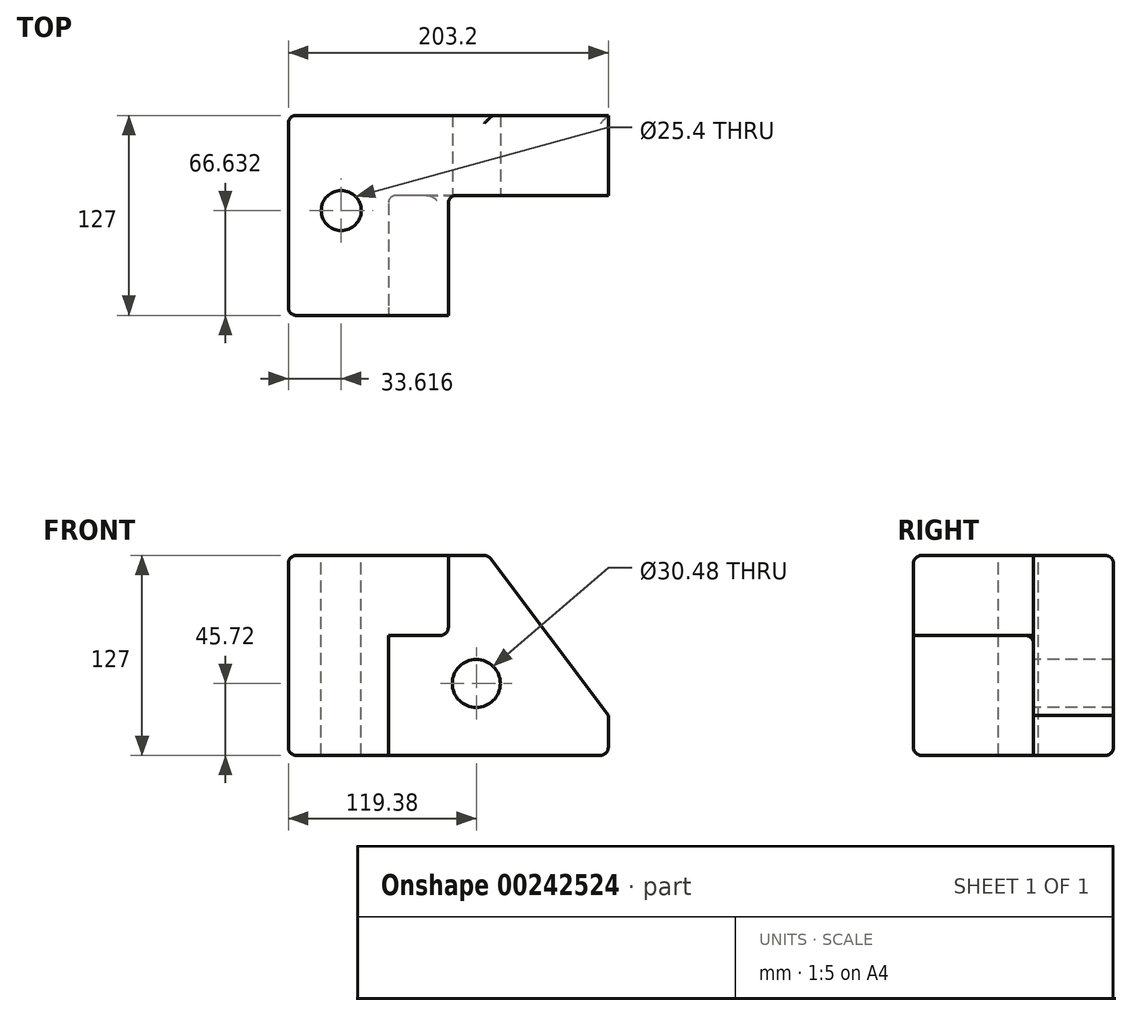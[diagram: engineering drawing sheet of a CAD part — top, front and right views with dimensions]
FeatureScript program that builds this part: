
annotation { "Feature Type Name" : "Feature", "Feature Type Description" : "" }
export const myFeature = defineFeature(function(context is Context, id is Id, definition is map)
    precondition{}
    {
        {
            var Q0;
            Q0=qCreatedBy(makeId("Front.planeOp"),FACE);
            var sketch = newSketch(context, id + "F0", { "sketchPlane" : qUnion([Q0])});
            skLineSegment(sketch, "E0.bottom", {"start": v(101.6, -63.5) * mm, "end": v(-101.6, -63.5) * mm});
            skLineSegment(sketch, "E0.top", {"start": v(101.6, 63.5) * mm, "end": v(-101.6, 63.5) * mm});
            skLineSegment(sketch, "E0.left", {"start": v(101.6, -63.5) * mm, "end": v(101.6, 63.5) * mm});
            skLineSegment(sketch, "E0.right", {"start": v(-101.6, -63.5) * mm, "end": v(-101.6, 63.5) * mm});
            skPoint(sketch, "E0.middle", {"position": v(0, 0) * mm});
            skSolve(sketch);
        }
        {
            var Q0;
            Q0 = qSketchRegion(id + "F0", true);
            extrude(context, id + "F1", {"entities" : qUnion([Q0]), "depth" : 127 * mm});
        }
        {
            var Q0;
            Q0=makeQuery(id+"F1.opExtrude","CAP_FACE",FACE,{"disambiguationData":[OSD([sQuery(id+"F0.wireOp",EDGE,"E0.bottom"),sQuery(id+"F0.wireOp",EDGE,"E0.top"),sQuery(id+"F0.wireOp",EDGE,"E0.left"),sQuery(id+"F0.wireOp",EDGE,"E0.right")])],"isStart":false});
            var sketch = newSketch(context, id + "F2", { "sketchPlane" : qUnion([Q0])});
            skLineSegment(sketch, "E1", {"start": v(-101.6, 63.5) * mm, "end": v(0, 63.5) * mm});
            skLineSegment(sketch, "E2", {"start": v(0, 63.5) * mm, "end": v(0, 12.7) * mm});
            skLineSegment(sketch, "E3", {"start": v(0, 12.7) * mm, "end": v(-38.1, 12.7) * mm});
            skLineSegment(sketch, "E4", {"start": v(-38.1, 12.7) * mm, "end": v(-38.1, -63.5) * mm});
            skLineSegment(sketch, "E5", {"start": v(-38.1, -63.5) * mm, "end": v(-101.6, -63.5) * mm});
            skLineSegment(sketch, "E6", {"start": v(-101.6, -63.5) * mm, "end": v(-101.6, 63.5) * mm});
            skSolve(sketch);
        }
        {
            var Q0;
            {var subQ3=sQuery(id+"F2.wireOp",EDGE,"E2");Q0=makeQuery(id+"F2.imprint","IMPRINT",FACE,{"disambiguationData":[TD([[makeQuery(id+"F2.imprint","IMPRINT",EDGE,{"derivedFrom":subQ3}),1.0]])]});}
            extrude(context, id + "F3", {"entities" : qUnion([Q0]), "operationType" : NewBodyOperationType.REMOVE, "oppositeDirection" : true, "depth" : 76.2 * mm});
        }
        {
            var Q0;
            Q0=makeQuery(id+"F1.opExtrude","SWEPT_EDGE",EDGE,{"disambiguationData":[OSD([sQuery(id+"F0.wireOp",EDGE,"E0.top"),sQuery(id+"F0.wireOp",EDGE,"E0.left")])]});
            chamfer(context, id + "F4", {"entities" : qUnion([Q0]), "chamferType" : ChamferType.TWO_OFFSETS, "width1" : 76.2 * mm, "oppositeDirection" : false, "width2" : 101.6 * mm, "tangentPropagation" : true});
        }
        {
            var Q0;
            Q0=makeQuery(id+"F3.boolean.opBoolean","COPY",EDGE,{"derivedFrom":makeQuery(id+"F3.opExtrude","SWEPT_EDGE",EDGE,{"disambiguationData":[OSD([sQuery(id+"F0.wireOp",EDGE,"E0.top"),sQuery(id+"F2.wireOp",EDGE,"E1"),sQuery(id+"F2.wireOp",EDGE,"E2")])]})});
            var Q1;
            Q1=makeQuery(id+"F3.boolean.opBoolean","COPY",EDGE,{"derivedFrom":makeQuery(id+"F3.opExtrude","CAP_EDGE",EDGE,{"disambiguationData":[OSD([sQuery(id+"F0.wireOp",EDGE,"E0.top")])],"isStart":false})});
            var Q2;
            {var subQ0=sQuery(id+"F0.wireOp",EDGE,"E0.top");Q2=makeQuery(id+"F4.opChamfer","BLEND_EDGE",EDGE,{"blendedFrom":[makeQuery(id+"F1.opExtrude","SWEPT_EDGE",EDGE,{"disambiguationData":[OSD([subQ0,sQuery(id+"F0.wireOp",EDGE,"E0.left")])]}),makeQuery(id+"F1.opExtrude","SWEPT_FACE",FACE,{"disambiguationData":[OSD([subQ0])]})],"blendedInto":[makeQuery(id+"F1.opExtrude","SWEPT_FACE",FACE,{"disambiguationData":[OSD([subQ0])]})]});}
            var Q3;
            Q3=makeQuery(id+"F1.opExtrude","CAP_EDGE",EDGE,{"disambiguationData":[OSD([sQuery(id+"F0.wireOp",EDGE,"E0.top")])],"isStart":true});
            var Q4;
            Q4=makeQuery(id+"F1.opExtrude","SWEPT_EDGE",EDGE,{"disambiguationData":[OSD([sQuery(id+"F0.wireOp",EDGE,"E0.top"),sQuery(id+"F0.wireOp",EDGE,"E0.right")])]});
            var Q5;
            Q5=makeQuery(id+"F1.opExtrude","CAP_EDGE",EDGE,{"disambiguationData":[OSD([sQuery(id+"F0.wireOp",EDGE,"E0.top")])],"isStart":false});
            var Q6;
            Q6=makeQuery(id+"F3.boolean.opBoolean","COPY",EDGE,{"derivedFrom":makeQuery(id+"F3.opExtrude","CAP_EDGE",EDGE,{"disambiguationData":[OSD([sQuery(id+"F2.wireOp",EDGE,"E2")])],"isStart":true})});
            var Q7;
            Q7=makeQuery(id+"F3.boolean.opBoolean","COPY",EDGE,{"derivedFrom":makeQuery(id+"F3.opExtrude","SWEPT_EDGE",EDGE,{"disambiguationData":[OSD([sQuery(id+"F2.wireOp",EDGE,"E2"),sQuery(id+"F2.wireOp",EDGE,"E3")])]})});
            var Q8;
            Q8=makeQuery(id+"F3.boolean.opBoolean","COPY",EDGE,{"derivedFrom":makeQuery(id+"F3.opExtrude","CAP_EDGE",EDGE,{"disambiguationData":[OSD([sQuery(id+"F2.wireOp",EDGE,"E2")])],"isStart":false})});
            var Q9;
            Q9=makeQuery(id+"F3.boolean.opBoolean","COPY",EDGE,{"derivedFrom":makeQuery(id+"F3.opExtrude","CAP_EDGE",EDGE,{"disambiguationData":[OSD([sQuery(id+"F2.wireOp",EDGE,"E4")])],"isStart":false})});
            var Q10;
            Q10=makeQuery(id+"F3.boolean.opBoolean","COPY",EDGE,{"derivedFrom":makeQuery(id+"F3.opExtrude","CAP_EDGE",EDGE,{"disambiguationData":[OSD([sQuery(id+"F2.wireOp",EDGE,"E4")])],"isStart":true})});
            var Q11;
            Q11=makeQuery(id+"F3.boolean.opBoolean","COPY",EDGE,{"derivedFrom":makeQuery(id+"F3.opExtrude","SWEPT_EDGE",EDGE,{"disambiguationData":[OSD([sQuery(id+"F0.wireOp",EDGE,"E0.bottom"),sQuery(id+"F2.wireOp",EDGE,"E4"),sQuery(id+"F2.wireOp",EDGE,"E5")])]})});
            var Q12;
            Q12=makeQuery(id+"F1.opExtrude","CAP_EDGE",EDGE,{"disambiguationData":[OSD([sQuery(id+"F0.wireOp",EDGE,"E0.bottom")])],"isStart":false});
            var Q13;
            Q13=makeQuery(id+"F1.opExtrude","CAP_EDGE",EDGE,{"disambiguationData":[OSD([sQuery(id+"F0.wireOp",EDGE,"E0.right")])],"isStart":false});
            var Q14;
            Q14=makeQuery(id+"F3.boolean.opBoolean","COPY",EDGE,{"derivedFrom":makeQuery(id+"F3.opExtrude","CAP_EDGE",EDGE,{"disambiguationData":[OSD([sQuery(id+"F0.wireOp",EDGE,"E0.bottom")])],"isStart":false})});
            var Q15;
            Q15=makeQuery(id+"F1.opExtrude","SWEPT_EDGE",EDGE,{"disambiguationData":[OSD([sQuery(id+"F0.wireOp",EDGE,"E0.bottom"),sQuery(id+"F0.wireOp",EDGE,"E0.left")])]});
            var Q16;
            Q16=makeQuery(id+"F1.opExtrude","SWEPT_EDGE",EDGE,{"disambiguationData":[OSD([sQuery(id+"F0.wireOp",EDGE,"E0.bottom"),sQuery(id+"F0.wireOp",EDGE,"E0.right")])]});
            var Q17;
            Q17=makeQuery(id+"F1.opExtrude","CAP_EDGE",EDGE,{"disambiguationData":[OSD([sQuery(id+"F0.wireOp",EDGE,"E0.right")])],"isStart":true});
            var Q18;
            Q18=makeQuery(id+"F1.opExtrude","CAP_EDGE",EDGE,{"disambiguationData":[OSD([sQuery(id+"F0.wireOp",EDGE,"E0.bottom")])],"isStart":true});
            fillet(context, id + "F5", {"entities" : qUnion([Q0, Q1, Q2, Q3, Q4, Q5, Q6, Q7, Q8, Q9, Q10, Q11, Q12, Q13, Q14, Q15, Q16, Q17, Q18]), "radius" : 5.08 * mm, "tangentPropagation" : true, "allowEdgeOverflow" : false});
        }
        {
            var Q0;
            Q0=makeQuery(id+"F3.boolean.opBoolean","COPY",FACE,{"derivedFrom":makeQuery(id+"F3.opExtrude","CAP_FACE",FACE,{"disambiguationData":[OSD([sQuery(id+"F0.wireOp",EDGE,"E0.bottom"),sQuery(id+"F0.wireOp",EDGE,"E0.top"),sQuery(id+"F0.wireOp",EDGE,"E0.left"),sQuery(id+"F2.wireOp",EDGE,"E2"),sQuery(id+"F2.wireOp",EDGE,"E3"),sQuery(id+"F2.wireOp",EDGE,"E4")])],"isStart":false})});
            var sketch = newSketch(context, id + "F6", { "sketchPlane" : qUnion([Q0])});
            skCircle(sketch, "E7", {"center": v(17.78, -17.78) * mm, "radius": 15.24 * mm});
            skSolve(sketch);
        }
        {
            var Q0;
            Q0=makeQuery(id+"F6.imprint","IMPRINT",FACE,{"disambiguationData":[TD([[makeQuery(id+"F6.imprint","IMPRINT",EDGE,{"derivedFrom":sQuery(id+"F6.wireOp",EDGE,"E7")}),1.0]])]});
            var Q1;
            Q1=makeQuery(id+"F1.opExtrude","CAP_FACE",FACE,{"disambiguationData":[OSD([sQuery(id+"F0.wireOp",EDGE,"E0.bottom"),sQuery(id+"F0.wireOp",EDGE,"E0.top"),sQuery(id+"F0.wireOp",EDGE,"E0.left"),sQuery(id+"F0.wireOp",EDGE,"E0.right")])],"isStart":true});
            extrude(context, id + "F7", {"entities" : qUnion([Q0]), "operationType" : NewBodyOperationType.REMOVE, "endBound" : BoundingType.UP_TO_SURFACE, "oppositeDirection" : true, "endBoundEntityFace" : qUnion([Q1]), "depth" : 25.4 * mm});
        }
        {
            var Q0;
            Q0=makeQuery(id+"F1.opExtrude","SWEPT_FACE",FACE,{"disambiguationData":[OSD([sQuery(id+"F0.wireOp",EDGE,"E0.top")])]});
            var sketch = newSketch(context, id + "F8", { "sketchPlane" : qUnion([Q0])});
            skCircle(sketch, "E8", {"center": v(-67.98, -60.37) * mm, "radius": 12.7 * mm});
            skSolve(sketch);
        }
        {
            var Q0;
            Q0=makeQuery(id+"F8.imprint","IMPRINT",FACE,{"disambiguationData":[TD([[makeQuery(id+"F8.imprint","IMPRINT",EDGE,{"derivedFrom":sQuery(id+"F8.wireOp",EDGE,"E8")}),1.0]])]});
            var Q1;
            Q1=makeQuery(id+"F1.opExtrude","SWEPT_FACE",FACE,{"disambiguationData":[OSD([sQuery(id+"F0.wireOp",EDGE,"E0.bottom")])]});
            extrude(context, id + "F9", {"entities" : qUnion([Q0]), "operationType" : NewBodyOperationType.REMOVE, "endBound" : BoundingType.UP_TO_SURFACE, "oppositeDirection" : true, "endBoundEntityFace" : qUnion([Q1]), "depth" : 25.4 * mm});
        }
    });
